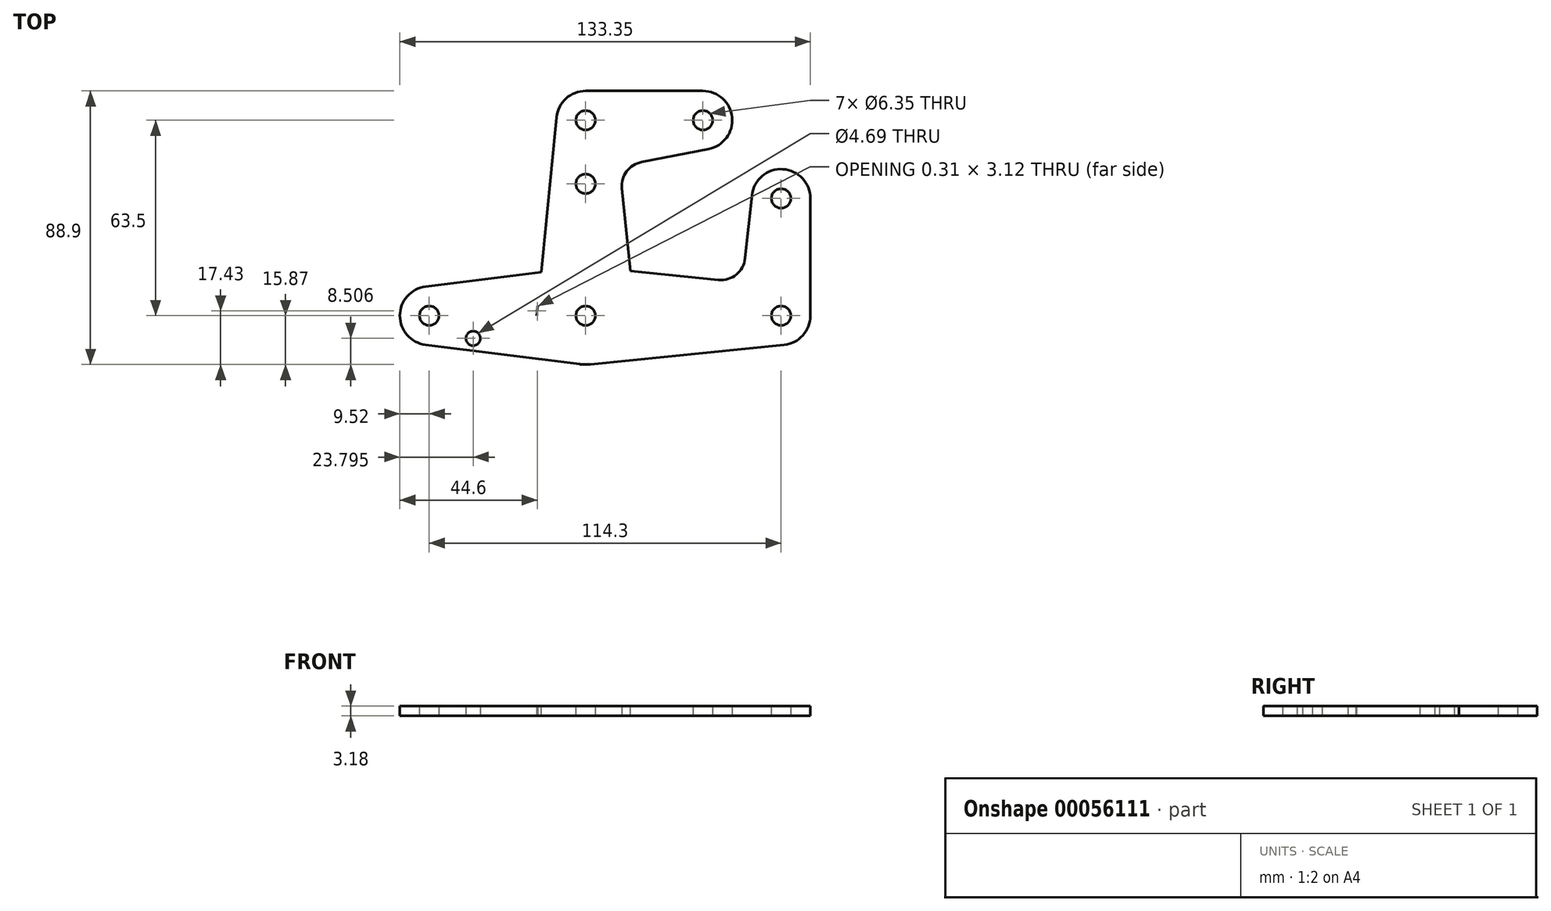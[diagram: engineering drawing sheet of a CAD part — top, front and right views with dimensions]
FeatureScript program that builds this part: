
annotation { "Feature Type Name" : "Feature", "Feature Type Description" : "" }
export const myFeature = defineFeature(function(context is Context, id is Id, definition is map)
    precondition{}
    {
        {
            var Q0;
            Q0=qCreatedBy(makeId("Top.planeOp"),FACE);
            var sketch = newSketch(context, id + "F0", { "sketchPlane" : qUnion([Q0])});
            skLineSegment(sketch, "E0", {"start": v(0, 0) * mm, "end": v(0, 63.5) * mm, "construction": true});
            skLineSegment(sketch, "E1", {"start": v(-50.8, 0) * mm, "end": v(63.5, 0) * mm, "construction": true});
            skLineSegment(sketch, "E2", {"start": v(0, 63.5) * mm, "end": v(38.1, 63.5) * mm, "construction": true});
            skLineSegment(sketch, "E3", {"start": v(63.5, 0) * mm, "end": v(63.5, 38.1) * mm, "construction": true});
            skCircle(sketch, "E4", {"center": v(0, 0) * mm, "radius": 3.18 * mm});
            skCircle(sketch, "E5", {"center": v(-50.8, 0) * mm, "radius": 3.18 * mm});
            skCircle(sketch, "E6", {"center": v(63.5, 0) * mm, "radius": 3.18 * mm});
            skCircle(sketch, "E7", {"center": v(0, 63.5) * mm, "radius": 3.18 * mm});
            skCircle(sketch, "E8", {"center": v(38.1, 63.5) * mm, "radius": 3.18 * mm});
            skCircle(sketch, "E9", {"center": v(63.5, 38.1) * mm, "radius": 3.18 * mm});
            skCircle(sketch, "E10", {"center": v(-50.8, 0) * mm, "radius": 9.53 * mm});
            skCircle(sketch, "E11", {"center": v(63.5, 0) * mm, "radius": 9.53 * mm});
            skCircle(sketch, "E12", {"center": v(63.5, 38.1) * mm, "radius": 9.52 * mm});
            skCircle(sketch, "E13", {"center": v(38.1, 63.5) * mm, "radius": 9.53 * mm});
            skCircle(sketch, "E14", {"center": v(0, 63.5) * mm, "radius": 9.53 * mm});
            skCircle(sketch, "E15", {"center": v(0, 0) * mm, "radius": 15.88 * mm});
            skLineSegment(sketch, "E16", {"start": v(-52, 9.45) * mm, "end": v(-1.98, 15.75) * mm});
            skLineSegment(sketch, "E17", {"start": v(-52, -9.45) * mm, "end": v(-1.98, -15.75) * mm});
            skLineSegment(sketch, "E18", {"start": v(64.45, -9.48) * mm, "end": v(1.59, -15.8) * mm});
            skLineSegment(sketch, "E19", {"start": v(-15.88, 0) * mm, "end": v(-9.48, 64.44) * mm});
            skLineSegment(sketch, "E20", {"start": v(73.02, 0) * mm, "end": v(73.02, 38.1) * mm});
            skLineSegment(sketch, "E21", {"start": v(0, 73.03) * mm, "end": v(38.1, 73.03) * mm});
            skCircle(sketch, "E22", {"center": v(0, 42.85) * mm, "radius": 3.18 * mm});
            skCircle(sketch, "E23", {"center": v(-36.53, -7.36) * mm, "radius": 2.35 * mm});
            skLineSegment(sketch, "E24", {"start": v(15.8, 1.59) * mm, "end": v(9.48, 64.45) * mm});
            skCircle(sketch, "E25", {"center": v(19.71, 42.11) * mm, "radius": 7.95 * mm});
            skLineSegment(sketch, "E26", {"start": v(39.92, 54.15) * mm, "end": v(18.2, 49.91) * mm});
            skLineSegment(sketch, "E27", {"start": v(1.59, 15.8) * mm, "end": v(64.45, 9.48) * mm});
            skCircle(sketch, "E28", {"center": v(43.91, 19.53) * mm, "radius": 7.95 * mm});
            skLineSegment(sketch, "E29", {"start": v(51.82, 18.68) * mm, "end": v(54.03, 39.12) * mm});
            skSolve(sketch);
        }
        {
            var Q0;
            Q0=makeQuery(id+"F0.imprint","IMPRINT",FACE,{"disambiguationData":[TD([[makeQuery(id+"F0.imprint","IMPRINT",EDGE,{"derivedFrom":sQuery(id+"F0.wireOp",EDGE,"E6")}),-1.0]])]});
            var Q1;
            {var subQ6=sQuery(id+"F0.wireOp",EDGE,"E18");Q1=makeQuery(id+"F0.imprint","IMPRINT",FACE,{"disambiguationData":[TD([[makeQuery(id+"F0.imprint","IMPRINT",EDGE,{"derivedFrom":subQ6}),-1.0]])]});}
            var Q2;
            {var subQ0=sQuery(id+"F0.wireOp",EDGE,"E24");var subQ1=sQuery(id+"F0.wireOp",EDGE,"E15");var subQ2=makeQuery(id+"F0.imprint","INTERSECT",VERTEX,{"derivedFrom":[subQ1,subQ0]});Q2=makeQuery(id+"F0.imprint","IMPRINT",FACE,{"disambiguationData":[TD([[makeQuery(id+"F0.imprint","IMPRINT",EDGE,{"disambiguationData":[TD([[subQ2,-1.0]])],"derivedFrom":subQ1}),-1.0]])]});}
            var Q3;
            Q3=makeQuery(id+"F0.imprint","IMPRINT",FACE,{"disambiguationData":[TD([[makeQuery(id+"F0.imprint","IMPRINT",EDGE,{"derivedFrom":sQuery(id+"F0.wireOp",EDGE,"E4")}),-1.0]])]});
            var Q4;
            {var subQ0=sQuery(id+"F0.wireOp",EDGE,"E16");var subQ1=sQuery(id+"F0.wireOp",EDGE,"E15");var subQ2=makeQuery(id+"F0.imprint","INTERSECT",VERTEX,{"derivedFrom":[subQ1,subQ0]});Q4=makeQuery(id+"F0.imprint","IMPRINT",FACE,{"disambiguationData":[TD([[makeQuery(id+"F0.imprint","IMPRINT",EDGE,{"disambiguationData":[TD([[subQ2,-1.0]])],"derivedFrom":subQ1}),-1.0]])]});}
            var Q5;
            {var subQ5=sQuery(id+"F0.wireOp",EDGE,"E17");Q5=makeQuery(id+"F0.imprint","IMPRINT",FACE,{"disambiguationData":[TD([[makeQuery(id+"F0.imprint","IMPRINT",EDGE,{"derivedFrom":subQ5}),1.0]])]});}
            var Q6;
            Q6=makeQuery(id+"F0.imprint","IMPRINT",FACE,{"disambiguationData":[TD([[makeQuery(id+"F0.imprint","IMPRINT",EDGE,{"derivedFrom":sQuery(id+"F0.wireOp",EDGE,"E5")}),-1.0]])]});
            var Q7;
            {var subQ0=sQuery(id+"F0.wireOp",EDGE,"E20");Q7=makeQuery(id+"F0.imprint","IMPRINT",FACE,{"disambiguationData":[TD([[makeQuery(id+"F0.imprint","IMPRINT",EDGE,{"derivedFrom":subQ0}),1.0]])]});}
            var Q8;
            Q8=makeQuery(id+"F0.imprint","IMPRINT",FACE,{"disambiguationData":[TD([[makeQuery(id+"F0.imprint","IMPRINT",EDGE,{"derivedFrom":sQuery(id+"F0.wireOp",EDGE,"E9")}),-1.0]])]});
            extrude(context, id + "F1", {"entities" : qUnion([Q0, Q1, Q2, Q3, Q4, Q5, Q6, Q7, Q8]), "depth" : 3.17 * mm});
        }
        {
            var Q0;
            Q0=makeQuery(id+"F0.imprint","IMPRINT",FACE,{"disambiguationData":[TD([[makeQuery(id+"F0.imprint","IMPRINT",EDGE,{"derivedFrom":sQuery(id+"F0.wireOp",EDGE,"E8")}),-1.0]])]});
            var Q1;
            {var subQ5=sQuery(id+"F0.wireOp",EDGE,"E21");Q1=makeQuery(id+"F0.imprint","IMPRINT",FACE,{"disambiguationData":[TD([[makeQuery(id+"F0.imprint","IMPRINT",EDGE,{"derivedFrom":subQ5}),-1.0]])]});}
            var Q2;
            Q2=makeQuery(id+"F0.imprint","IMPRINT",FACE,{"disambiguationData":[TD([[makeQuery(id+"F0.imprint","IMPRINT",EDGE,{"derivedFrom":sQuery(id+"F0.wireOp",EDGE,"E7")}),-1.0]])]});
            var Q3;
            Q3=makeQuery(id+"F0.imprint","IMPRINT",FACE,{"disambiguationData":[TD([[makeQuery(id+"F0.imprint","IMPRINT",EDGE,{"derivedFrom":sQuery(id+"F0.wireOp",EDGE,"E22")}),-1.0]])]});
            var Q4;
            Q4=makeQuery(id+"F0.imprint","IMPRINT",FACE,{"disambiguationData":[TD([[makeQuery(id+"F0.imprint","IMPRINT",EDGE,{"derivedFrom":sQuery(id+"F0.wireOp",EDGE,"E4")}),-1.0]])]});
            var Q5;
            {var subQ0=sQuery(id+"F0.wireOp",EDGE,"E24");var subQ1=sQuery(id+"F0.wireOp",EDGE,"E15");var subQ2=makeQuery(id+"F0.imprint","INTERSECT",VERTEX,{"derivedFrom":[subQ1,subQ0]});Q5=makeQuery(id+"F0.imprint","IMPRINT",FACE,{"disambiguationData":[TD([[makeQuery(id+"F0.imprint","IMPRINT",EDGE,{"disambiguationData":[TD([[subQ2,-1.0]])],"derivedFrom":subQ1}),-1.0]])]});}
            var Q6;
            {var subQ0=sQuery(id+"F0.wireOp",EDGE,"E16");var subQ1=sQuery(id+"F0.wireOp",EDGE,"E15");var subQ2=makeQuery(id+"F0.imprint","INTERSECT",VERTEX,{"derivedFrom":[subQ1,subQ0]});Q6=makeQuery(id+"F0.imprint","IMPRINT",FACE,{"disambiguationData":[TD([[makeQuery(id+"F0.imprint","IMPRINT",EDGE,{"disambiguationData":[TD([[subQ2,-1.0]])],"derivedFrom":subQ1}),-1.0]])]});}
            extrude(context, id + "F2", {"entities" : qUnion([Q0, Q1, Q2, Q3, Q4, Q5, Q6]), "operationType" : NewBodyOperationType.ADD, "depth" : 3.17 * mm});
        }
    });
